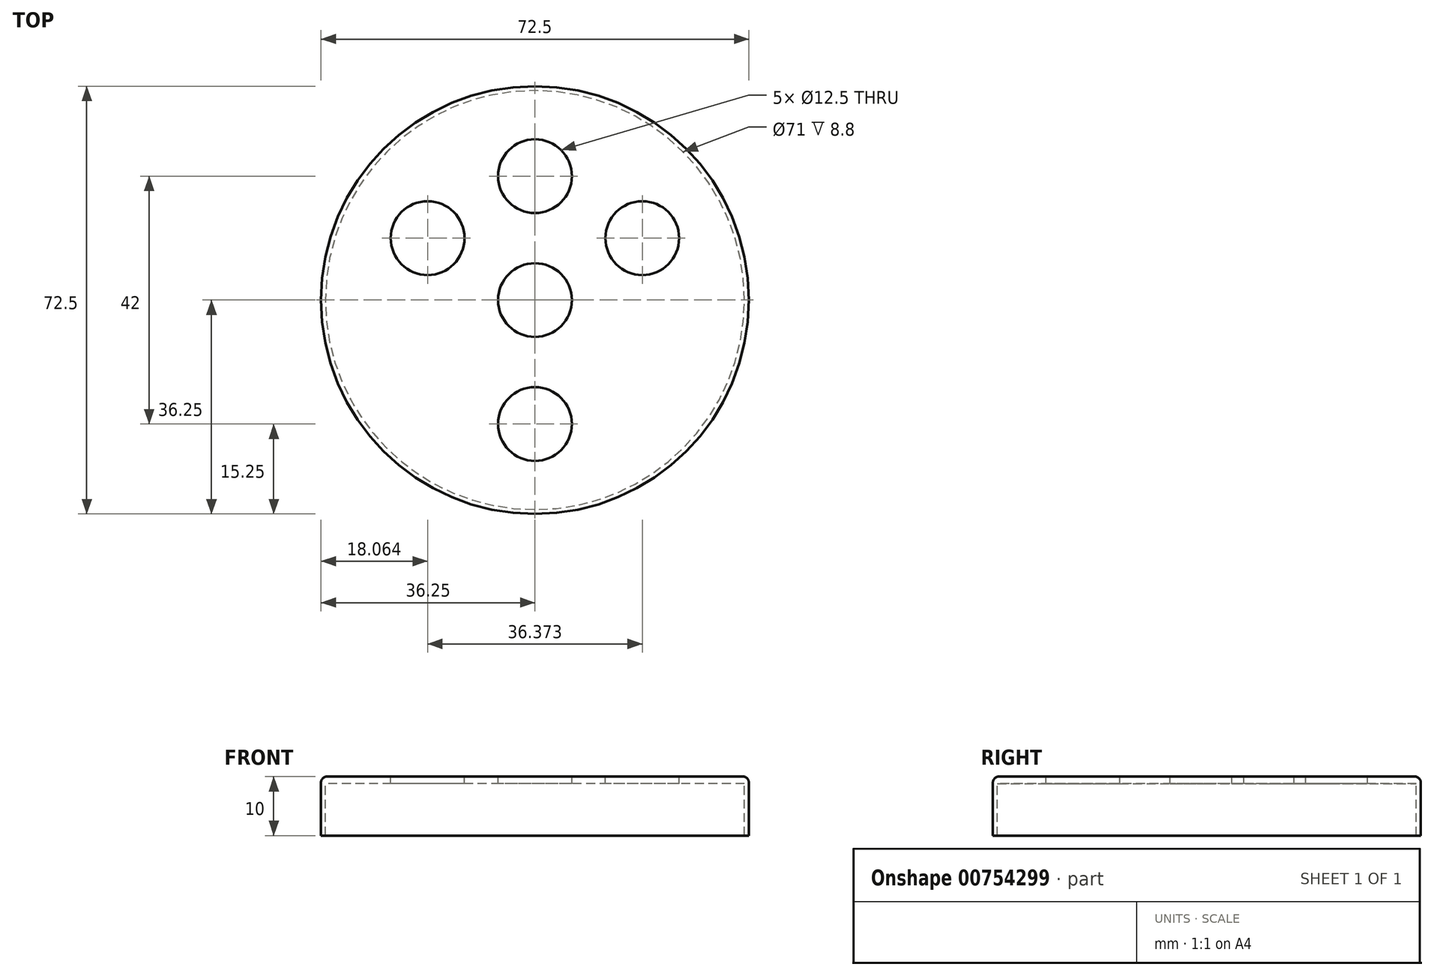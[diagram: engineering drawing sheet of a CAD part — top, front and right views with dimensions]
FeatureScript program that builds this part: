
annotation { "Feature Type Name" : "Feature", "Feature Type Description" : "" }
export const myFeature = defineFeature(function(context is Context, id is Id, definition is map)
    precondition{}
    {
        {
            var Q0;
            Q0=qCreatedBy(makeId("Top.planeOp"),FACE);
            var sketch = newSketch(context, id + "F0", { "sketchPlane" : qUnion([Q0])});
            skCircle(sketch, "E0", {"center": v(0, 0) * mm, "radius": 36.25 * mm});
            skCircle(sketch, "E1", {"center": v(0, 0) * mm, "radius": 6.25 * mm});
            skCircle(sketch, "E2", {"center": v(0, 0) * mm, "radius": 21 * mm, "construction": true});
            skLineSegment(sketch, "E3", {"start": v(0, 0) * mm, "end": v(0, 45.67) * mm, "construction": true});
            skCircle(sketch, "E4", {"center": v(0, 21) * mm, "radius": 6.25 * mm});
            skCircle(sketch, "E5.1.1", {"center": v(-18.19, 10.5) * mm, "radius": 6.25 * mm});
            skCircle(sketch, "E6.2.3.0", {"center": v(0, -21) * mm, "radius": 6.25 * mm});
            skCircle(sketch, "E6.2.5.0", {"center": v(18.19, 10.5) * mm, "radius": 6.25 * mm});
            skCircle(sketch, "E7", {"center": v(0, 0) * mm, "radius": 35.5 * mm});
            skSolve(sketch);
        }
        {
            var Q0;
            Q0=makeQuery(id+"F0.imprint","IMPRINT",FACE,{"disambiguationData":[TD([[makeQuery(id+"F0.imprint","IMPRINT",EDGE,{"derivedFrom":sQuery(id+"F0.wireOp",EDGE,"E1")}),-1.0]])]});
            extrude(context, id + "F1", {"entities" : qUnion([Q0]), "oppositeDirection" : true, "depth" : 1.2 * mm, "offsetDistance" : 25 * mm});
        }
        {
            var Q0;
            Q0=makeQuery(id+"F0.imprint","IMPRINT",FACE,{"disambiguationData":[TD([[makeQuery(id+"F0.imprint","IMPRINT",EDGE,{"derivedFrom":sQuery(id+"F0.wireOp",EDGE,"E0")}),1.0]])]});
            extrude(context, id + "F2", {"entities" : qUnion([Q0]), "operationType" : NewBodyOperationType.ADD, "oppositeDirection" : true, "depth" : 10 * mm, "offsetDistance" : 25 * mm});
        }
        {
            var Q0;
            Q0=makeQuery(id+"F2.opExtrude","CAP_EDGE",EDGE,{"disambiguationData":[OSD([sQuery(id+"F0.wireOp",EDGE,"E0")])],"isStart":true});
            var Q1;
            Q1=makeQuery(id+"F1.opExtrude","CAP_EDGE",EDGE,{"disambiguationData":[OSD([sQuery(id+"F0.wireOp",EDGE,"E7")])],"isStart":false});
            fillet(context, id + "F3", {"entities" : qUnion([Q0, Q1]), "radius" : 1 * mm, "tangentPropagation" : true, "allowEdgeOverflow" : false});
        }
    });
